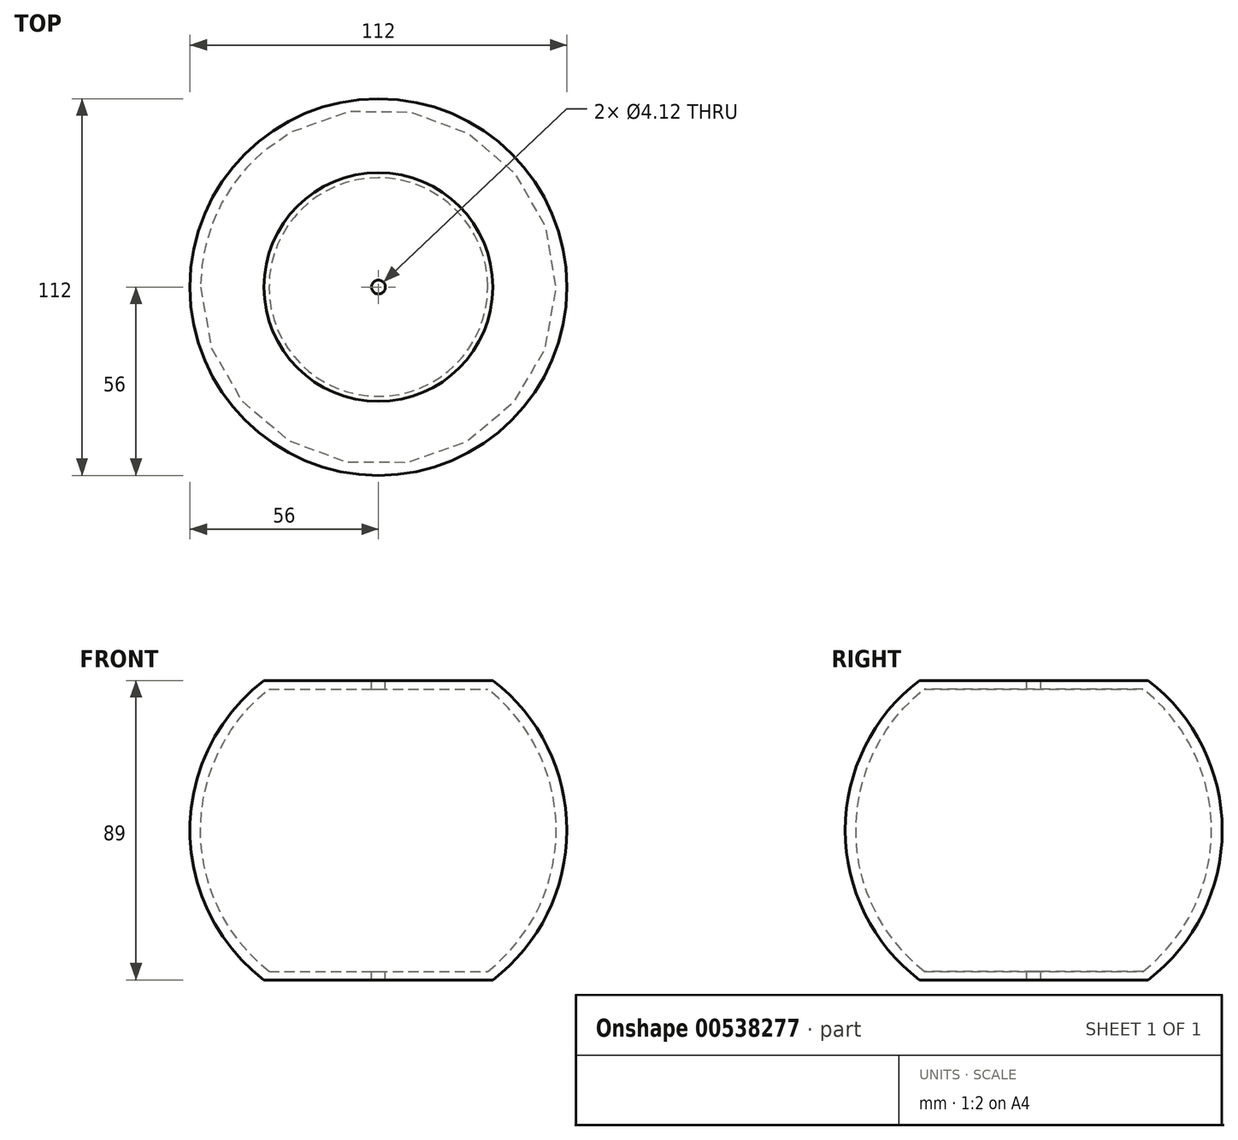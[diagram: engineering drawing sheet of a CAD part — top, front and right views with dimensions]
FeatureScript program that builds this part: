
annotation { "Feature Type Name" : "Feature", "Feature Type Description" : "" }
export const myFeature = defineFeature(function(context is Context, id is Id, definition is map)
    precondition{}
    {
        {
            var Q0;
            Q0=qCreatedBy(makeId("Front.planeOp"),FACE);
            var sketch = newSketch(context, id + "F0", { "sketchPlane" : qUnion([Q0])});
            skLineSegment(sketch, "E0", {"start": v(0, 42) * mm, "end": v(0, 44.5) * mm});
            skLineSegment(sketch, "E1", {"start": v(0, 44.5) * mm, "end": v(-34, 44.5) * mm});
            skLineSegment(sketch, "E2", {"start": v(0, -42) * mm, "end": v(0, -44.5) * mm});
            skLineSegment(sketch, "E3", {"start": v(0, -44.5) * mm, "end": v(-34, -44.5) * mm});
            skArc(sketch, "E4", {"start": v(-34, 44.5) * mm, "mid": v(-56, 0) * mm, "end": v(-34, -44.5) * mm});
            skLineSegment(sketch, "E5", {"start": v(0, 42) * mm, "end": v(-32.5, 42) * mm});
            skLineSegment(sketch, "E6", {"start": v(0, -42) * mm, "end": v(-32.5, -42) * mm});
            skArc(sketch, "E7", {"start": v(-32.5, 42) * mm, "mid": v(-52.83, 0) * mm, "end": v(-32.5, -42) * mm});
            skSolve(sketch);
        }
        {
            var Q0;
            Q0=makeQuery(id+"F0.imprint","IMPRINT",FACE,{"disambiguationData":[TD([[makeQuery(id+"F0.imprint","IMPRINT",EDGE,{"derivedFrom":sQuery(id+"F0.wireOp",EDGE,"E0")}),1.0]])]});
            var Q1;
            Q1=sQuery(id+"F0.wireOp",EDGE,"E0");
            revolve(context, id + "F1", {"surfaceOperationType" : NewSurfaceOperationType.NEW, "entities" : qUnion([Q0]), "axis" : qUnion([Q1]), "revolveType" : RevolveType.FULL});
        }
        {
            var Q0;
            Q0=makeQuery(id+"F1.opRevolve","SWEPT_FACE",FACE,{"disambiguationData":[OSD([sQuery(id+"F0.wireOp",EDGE,"E1")])]});
            var sketch = newSketch(context, id + "F2", { "sketchPlane" : qUnion([Q0])});
            skCircle(sketch, "E8", {"center": v(0, 0) * mm, "radius": 2.06 * mm});
            skSolve(sketch);
        }
        {
            var Q0;
            Q0=makeQuery(id+"F2.imprint","IMPRINT",FACE,{"disambiguationData":[TD([[makeQuery(id+"F2.imprint","IMPRINT",EDGE,{"derivedFrom":sQuery(id+"F2.wireOp",EDGE,"E8")}),1.0]])]});
            extrude(context, id + "F3", {"entities" : qUnion([Q0]), "operationType" : NewBodyOperationType.REMOVE, "endBound" : BoundingType.THROUGH_ALL, "oppositeDirection" : true, "depth" : 25 * mm, "offsetDistance" : 25 * mm});
        }
    });
